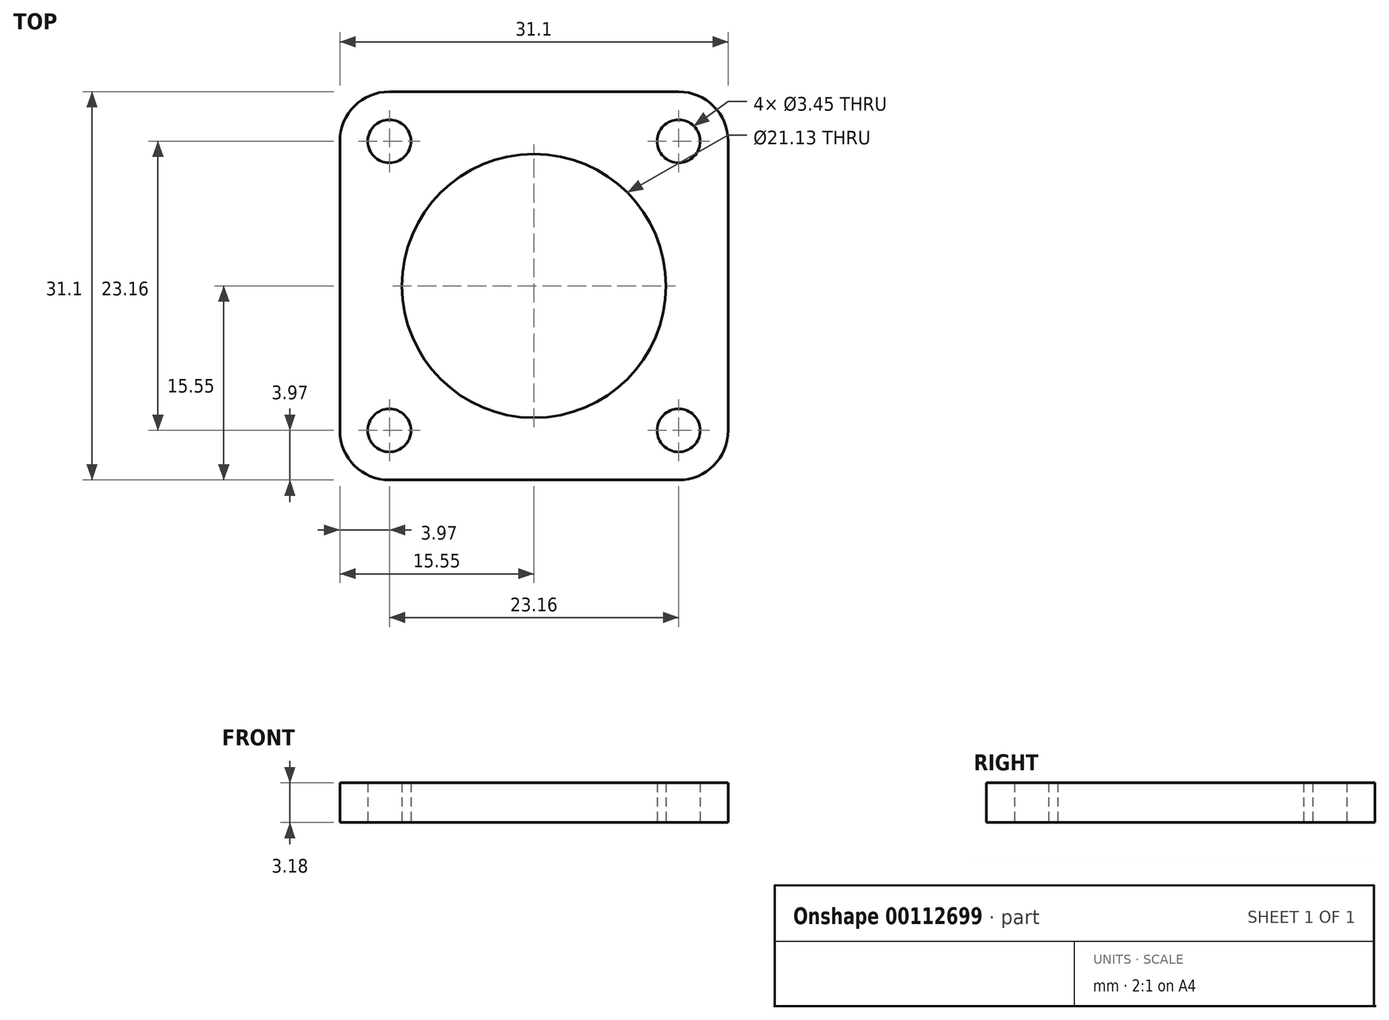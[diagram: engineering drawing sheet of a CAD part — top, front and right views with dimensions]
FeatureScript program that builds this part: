
annotation { "Feature Type Name" : "Feature", "Feature Type Description" : "" }
export const myFeature = defineFeature(function(context is Context, id is Id, definition is map)
    precondition{}
    {
        {
            var Q0;
            Q0=qCreatedBy(makeId("Top.planeOp"),FACE);
            var sketch = newSketch(context, id + "F0", { "sketchPlane" : qUnion([Q0])});
            skLineSegment(sketch, "E0.bottom", {"start": v(11.58, -11.58) * mm, "end": v(-11.58, -11.58) * mm, "construction": true});
            skLineSegment(sketch, "E0.top", {"start": v(11.58, 11.58) * mm, "end": v(-11.58, 11.58) * mm, "construction": true});
            skLineSegment(sketch, "E0.left", {"start": v(11.58, -11.58) * mm, "end": v(11.58, 11.58) * mm, "construction": true});
            skLineSegment(sketch, "E0.right", {"start": v(-11.58, -11.58) * mm, "end": v(-11.58, 11.58) * mm, "construction": true});
            skPoint(sketch, "E0.middle", {"position": v(0, 0) * mm});
            skCircle(sketch, "E1", {"center": v(0, 0) * mm, "radius": 10.57 * mm});
            skCircle(sketch, "E2", {"center": v(11.58, 11.58) * mm, "radius": 1.73 * mm});
            skCircle(sketch, "E3", {"center": v(-11.58, 11.58) * mm, "radius": 1.73 * mm});
            skCircle(sketch, "E4", {"center": v(-11.58, -11.58) * mm, "radius": 1.73 * mm});
            skCircle(sketch, "E5", {"center": v(11.58, -11.58) * mm, "radius": 1.73 * mm});
            skLineSegment(sketch, "E6.top", {"start": v(-15.55, 15.55) * mm, "end": v(15.55, 15.55) * mm});
            skLineSegment(sketch, "E6.left", {"start": v(-15.55, -15.55) * mm, "end": v(-15.55, 15.55) * mm});
            skLineSegment(sketch, "E6.right", {"start": v(15.55, -15.55) * mm, "end": v(15.55, 15.55) * mm});
            skLineSegment(sketch, "E7", {"start": v(0, 0) * mm, "end": v(0, 15.55) * mm, "construction": true});
            skLineSegment(sketch, "E8", {"start": v(-15.55, -15.55) * mm, "end": v(15.55, -15.55) * mm});
            skLineSegment(sketch, "E9", {"start": v(0, 0) * mm, "end": v(0, -15.55) * mm, "construction": true});
            skSolve(sketch);
        }
        {
            var Q0;
            Q0=qSketchRegion(id+"F0",true);
            extrude(context, id + "F1", {"entities" : qUnion([Q0]), "depth" : 3.17 * mm});
        }
        {
            var Q0;
            Q0=makeQuery(id+"F1.opExtrude","SWEPT_EDGE",EDGE,{"disambiguationData":[OSD([sQuery(id+"F0.wireOp",EDGE,"E6.left"),sQuery(id+"F0.wireOp",EDGE,"E8")])]});
            var Q1;
            Q1=makeQuery(id+"F1.opExtrude","SWEPT_EDGE",EDGE,{"disambiguationData":[OSD([sQuery(id+"F0.wireOp",EDGE,"E6.right"),sQuery(id+"F0.wireOp",EDGE,"E8")])]});
            var Q2;
            Q2=makeQuery(id+"F1.opExtrude","SWEPT_EDGE",EDGE,{"disambiguationData":[OSD([sQuery(id+"F0.wireOp",EDGE,"E6.top"),sQuery(id+"F0.wireOp",EDGE,"E6.right")])]});
            var Q3;
            Q3=makeQuery(id+"F1.opExtrude","SWEPT_EDGE",EDGE,{"disambiguationData":[OSD([sQuery(id+"F0.wireOp",EDGE,"E6.top"),sQuery(id+"F0.wireOp",EDGE,"E6.left")])]});
            fillet(context, id + "F2", {"entities" : qUnion([Q0, Q1, Q2, Q3]), "radius" : 3.97 * mm, "tangentPropagation" : true, "allowEdgeOverflow" : false});
        }
    });
